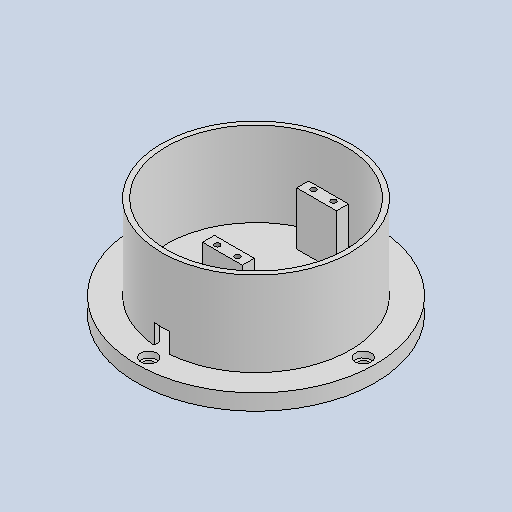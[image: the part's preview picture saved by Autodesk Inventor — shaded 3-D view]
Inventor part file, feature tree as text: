
AUTODESK INVENTOR PART (.ipt)
format: ipt  version: 2022 (Build 260153000, 153)  size: 350,208 bytes
history: native  units: in
note: dims shown in document units (in); Inventor stores cm internally (conversion verified against a paired STEP export)
features: extrude x19, sketch x19, thread x4
ambient origin geometry x8: Origin, YZ Plane, XZ Plane, XY Plane, X Axis, Y Axis, Z Axis, Center Point
bodies: Solid1 (feature_tree)
feature tree (42):
  extrude  "Extrusion1"  Depth=0.315in TaperAngle=0.0deg
  extrude  "Extrusion2"  Depth=0.1969in
  extrude  "Extrusion3"  Depth=0.1969in
  extrude  "Extrusion4"  Depth=0.1969in
  extrude  "Extrusion5"  Depth=0.1969in
  extrude  "Extrusion6"  Depth=0.315in
  extrude  "Extrusion7"  Depth=0.1969in
  extrude  "Extrusion8"  Depth=0.1969in
  extrude  "Extrusion9"  Depth=0.1181in TaperAngle=0.0deg
  extrude  "Extrusion10"  Depth=3.5433in
  extrude  "Extrusion11"  Depth=0.3937in
  extrude  "Extrusion12"  Depth=0.7874in
  thread  "Thread1"  [1 undecoded]
  thread  "Thread2"  [1 undecoded]
  thread  "Thread3"  [1 undecoded]
  thread  "Thread4"  [1 undecoded]
  extrude  "Extrusion13"  Depth=1.5748in
  extrude  "Extrusion14"  Depth=0.315in
  extrude  "Extrusion15"  Depth=0.315in TaperAngle=0.0deg
  extrude  "Extrusion16"  Depth=0.1575in
  extrude  "Extrusion17"  Depth=0.8661in TaperAngle=0.0deg
  extrude  "Extrusion18"  Depth=0.1969in
  extrude  "Extrusion19"  Depth=0.1575in
  sketch  "Sketch1"  dims[d0=4.7244in d1=0.315in d2=0.0in]
  sketch  "Sketch2"  dims[d3=0.315in d4=0.1969in]
  sketch  "Sketch3"  dims[d5=0.315in d6=0.1969in]
  sketch  "Sketch4"  dims[d7=0.315in d8=0.1969in]
  sketch  "Sketch5"  dims[d9=0.315in d10=0.1969in]
  sketch  "Sketch6"  dims[d11=0.315in d12=0.0in d13=0.315in]
  sketch  "Sketch7"  dims[d14=0.315in d15=0.1969in]
  sketch  "Sketch8"  dims[d16=0.315in d17=0.1969in]
  sketch  "Sketch9"  dims[d18=0.315in d19=0.1181in d20=0.0in]
  sketch  "Sketch10"  dims[d21=3.7402in d22=3.5433in]
  sketch  "Sketch11"  dims[d23=0.3937in d24=0.3543in]
  sketch  "Sketch12"  dims[d25=0.3937in d26=0.2756in d27=0.3937in d28=0.0in d29=0.3937in d30=0.3543in d31=0.7874in]
  sketch  "Sketch13"  dims[d32=0.2756in d33=1.5748in]
  sketch  "Sketch14"  dims[d34=0.315in d35=0.315in]
  sketch  "Sketch16"  dims[d36=0.315in d37=1.1024in d38=0.0in]
  sketch  "Sketch17"  dims[d39=0.1575in d40=0.1575in]
  sketch  "Sketch18"  dims[d41=1.1024in d42=0.0in d43=0.8661in d44=0.0in]
  sketch  "Sketch19"  dims[d45=0.0787in d46=0.1969in]
  sketch  "Sketch20"  dims[d47=0.1969in d48=0.1575in d49=0.1575in d50=0.0787in d51=0.1575in d52=0.1575in d53=0.3937in d54=0.0in d55=1.1024in d56=0.0in d57=0.3937in d58=1.437in d59=0.6654in d60=0.3937in d61=0.2362in d62=0.2362in d63=0.2362in d64=0.2362in d65=0.3937in d66=0.0in d67=0.6575in d68=0.0in d69=0.1004in d70=0.1004in d71=0.1988in d72=0.1988in d73=0.1988in d74=0.1988in d75=0.1063in d76=0.1063in d77=0.1063in d78=0.1063in d79=0.3937in d80=0.0in d81=0.3937in d82=0.0in d83=0.3937in d84=0.0in d85=0.3937in d86=0.0in d87=0.3937in d88=0.0in d89=1.8622in d90=0.0in d91=1.6732in d92=0.0in d93=1.6732in d94=0.0in d95=0.315in d96=0.0in d97=3.7402in d98=3.5433in d99=1.6732in d100=0.0in d101=2.0187in d102=0.0in d103=3.2313in d104=0.0in]
note: 4 required parameter values undecoded (feature->parameter linkage not recoverable at this tier; creation-order binding heuristic only, values carry confidence <= 0.55)
